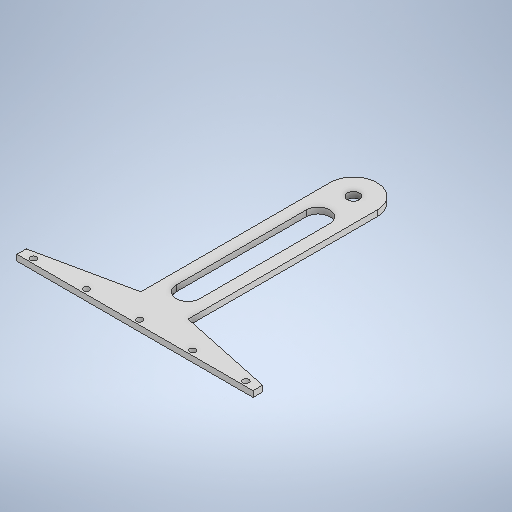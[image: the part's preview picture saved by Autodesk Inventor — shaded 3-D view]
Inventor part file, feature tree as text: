
AUTODESK INVENTOR PART (.ipt)
format: ipt  version: 2025.1 (Build 291241000, 241)  size: 293,376 bytes
history: native  units: mm
features: sketch x4, extrude x2, hole x2
ambient origin geometry x8: Origin, YZ Plane, XZ Plane, XY Plane, X Axis, Y Axis, Z Axis, Center Point
bodies: Solid1 (feature_tree)
feature tree (8):
  extrude  "Extrusion1"  Depth=20.0mm
  extrude  "Extrusion2"  Depth=25.0mm
  hole  "Hole1"  [1 undecoded]
  hole  "Hole2"  [1 undecoded]
  sketch  "Sketch1"  dims[d0=20.0mm d1=185.0mm]
  sketch  "Sketch2"  dims[d2=8.0mm d3=25.0mm]
  sketch  "Sketch3"  dims[d4=200.0mm d5=5.0mm d6=0.0mm]
  sketch  "Sketch4"  dims[d7=30.0mm d8=10.0mm d9=110.0mm d10=5.0mm d11=0.0mm d12=45.0mm d13=45.0mm d14=45.0mm d15=45.0mm d16=4.0mm d17=5.0mm d18=6.0mm d19=4.0mm d20=2.0mm d21=90.0deg d22=8.0mm d23=0.0mm d24=10.0mm d25=8.0mm d26=4.0mm d27=2.0mm d28=90.0deg d29=8.0mm d30=0.0mm]
note: 2 required parameter values undecoded (feature->parameter linkage not recoverable at this tier; creation-order binding heuristic only, values carry confidence <= 0.55)
